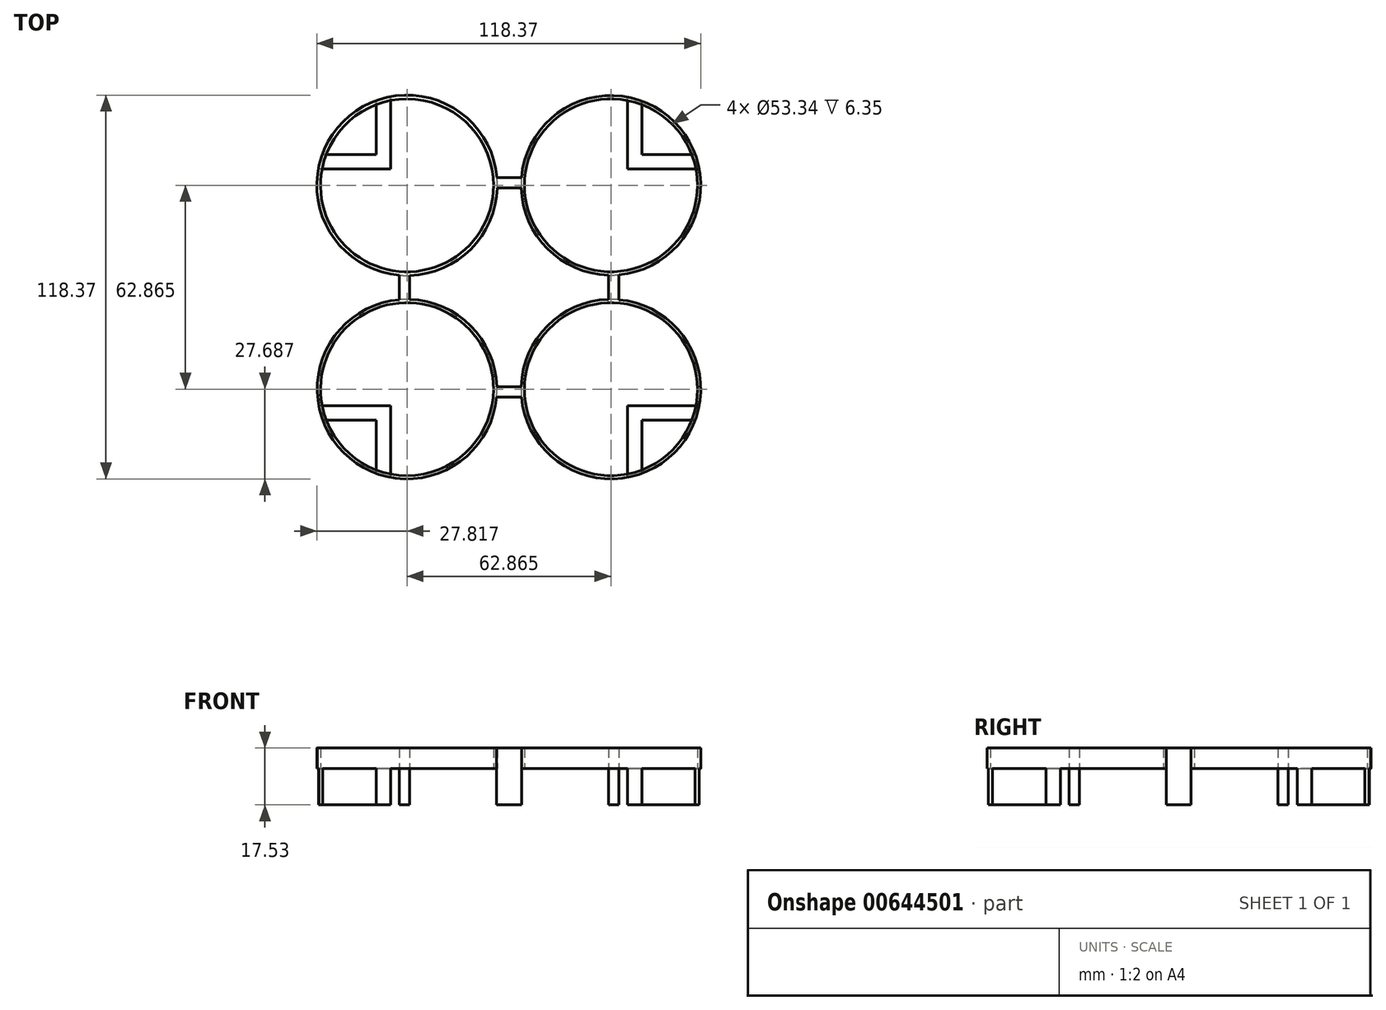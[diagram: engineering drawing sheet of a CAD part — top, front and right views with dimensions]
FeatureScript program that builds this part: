
annotation { "Feature Type Name" : "Feature", "Feature Type Description" : "" }
export const myFeature = defineFeature(function(context is Context, id is Id, definition is map)
    precondition{}
    {
        {
            var Q0;
            Q0=qCreatedBy(makeId("Top.planeOp"),FACE);
            var sketch = newSketch(context, id + "F0", { "sketchPlane" : qUnion([Q0])});
            skCircle(sketch, "E0", {"center": v(-31.43, 31.43) * mm, "radius": 26.67 * mm});
            skCircle(sketch, "E1", {"center": v(31.43, 31.43) * mm, "radius": 26.67 * mm});
            skCircle(sketch, "E2", {"center": v(31.43, -31.43) * mm, "radius": 26.67 * mm});
            skCircle(sketch, "E3", {"center": v(-31.43, -31.43) * mm, "radius": 26.67 * mm});
            skCircle(sketch, "E4", {"center": v(-31.43, 31.43) * mm, "radius": 27.81 * mm});
            skCircle(sketch, "E5", {"center": v(31.43, 31.43) * mm, "radius": 27.69 * mm});
            skCircle(sketch, "E6", {"center": v(31.43, -31.43) * mm, "radius": 27.69 * mm});
            skCircle(sketch, "E7", {"center": v(-31.43, -31.43) * mm, "radius": 27.69 * mm});
            skLineSegment(sketch, "E8.bottom", {"start": v(33.81, 33.81) * mm, "end": v(-33.81, 33.81) * mm});
            skLineSegment(sketch, "E8.top", {"start": v(33.81, -33.81) * mm, "end": v(-33.81, -33.81) * mm});
            skLineSegment(sketch, "E8.left", {"start": v(33.81, 33.81) * mm, "end": v(33.81, -33.81) * mm});
            skLineSegment(sketch, "E8.right", {"start": v(-33.81, 33.81) * mm, "end": v(-33.81, -33.81) * mm});
            skPoint(sketch, "E8.middle", {"position": v(0, 0) * mm});
            skLineSegment(sketch, "E9.bottom", {"start": v(30.64, 30.64) * mm, "end": v(-30.64, 30.64) * mm});
            skLineSegment(sketch, "E9.top", {"start": v(30.64, -30.64) * mm, "end": v(-30.64, -30.64) * mm});
            skLineSegment(sketch, "E9.left", {"start": v(30.64, 30.64) * mm, "end": v(30.64, -30.64) * mm});
            skLineSegment(sketch, "E9.right", {"start": v(-30.64, 30.64) * mm, "end": v(-30.64, -30.64) * mm});
            skSolve(sketch);
        }
        {
            var Q0;
            Q0 = qSketchRegion(id + "F0", true);
            var Q1;
            {var subQ0=sQuery(id+"F0.wireOp",EDGE,"E9.right");var subQ1=sQuery(id+"F0.wireOp",EDGE,"E0");var subQ2=makeQuery(id+"F0.imprint","INTERSECT",VERTEX,{"derivedFrom":[subQ1,subQ0]});Q1=makeQuery(id+"F0.imprint","IMPRINT",FACE,{"disambiguationData":[TD([[makeQuery(id+"F0.imprint","IMPRINT",EDGE,{"disambiguationData":[TD([[subQ2,-1.0]])],"derivedFrom":subQ1}),-1.0]])]});}
            var Q2;
            {var subQ0=sQuery(id+"F0.wireOp",EDGE,"E9.right");var subQ1=sQuery(id+"F0.wireOp",EDGE,"E3");var subQ2=makeQuery(id+"F0.imprint","INTERSECT",VERTEX,{"derivedFrom":[subQ1,subQ0]});Q2=makeQuery(id+"F0.imprint","IMPRINT",FACE,{"disambiguationData":[TD([[makeQuery(id+"F0.imprint","IMPRINT",EDGE,{"disambiguationData":[TD([[subQ2,1.0]])],"derivedFrom":subQ1}),-1.0]])]});}
            var Q3;
            {var subQ0=sQuery(id+"F0.wireOp",EDGE,"E9.left");var subQ1=sQuery(id+"F0.wireOp",EDGE,"E2");var subQ2=makeQuery(id+"F0.imprint","INTERSECT",VERTEX,{"derivedFrom":[subQ1,subQ0]});Q3=makeQuery(id+"F0.imprint","IMPRINT",FACE,{"disambiguationData":[TD([[makeQuery(id+"F0.imprint","IMPRINT",EDGE,{"disambiguationData":[TD([[subQ2,-1.0]])],"derivedFrom":subQ1}),-1.0]])]});}
            var Q4;
            {var subQ0=sQuery(id+"F0.wireOp",EDGE,"E9.bottom");var subQ1=sQuery(id+"F0.wireOp",EDGE,"E1");var subQ2=makeQuery(id+"F0.imprint","INTERSECT",VERTEX,{"derivedFrom":[subQ1,subQ0]});Q4=makeQuery(id+"F0.imprint","IMPRINT",FACE,{"disambiguationData":[TD([[makeQuery(id+"F0.imprint","IMPRINT",EDGE,{"disambiguationData":[TD([[subQ2,-1.0]])],"derivedFrom":subQ1}),-1.0]])]});}
            extrude(context, id + "F1", {"entities" : qUnion([Q0, Q1, Q2, Q3, Q4]), "depth" : 6.35 * mm, "offsetDistance" : 25.4 * mm});
        }
        {
            var Q0;
            {var subQ0=sQuery(id+"F0.wireOp",EDGE,"E8.top");var subQ1=sQuery(id+"F0.wireOp",EDGE,"E6");var subQ2=makeQuery(id+"F0.imprint","INTERSECT",VERTEX,{"derivedFrom":[subQ1,subQ0]});Q0=makeQuery(id+"F0.imprint","IMPRINT",FACE,{"disambiguationData":[TD([[makeQuery(id+"F0.imprint","IMPRINT",EDGE,{"disambiguationData":[TD([[subQ2,1.0]])],"derivedFrom":subQ1}),-1.0]])]});}
            var Q1;
            {var subQ0=sQuery(id+"F0.wireOp",EDGE,"E8.right");var subQ1=sQuery(id+"F0.wireOp",EDGE,"E4");var subQ2=makeQuery(id+"F0.imprint","INTERSECT",VERTEX,{"derivedFrom":[subQ1,subQ0]});Q1=makeQuery(id+"F0.imprint","IMPRINT",FACE,{"disambiguationData":[TD([[makeQuery(id+"F0.imprint","IMPRINT",EDGE,{"disambiguationData":[TD([[subQ2,-1.0]])],"derivedFrom":subQ1}),-1.0]])]});}
            var Q2;
            {var subQ0=sQuery(id+"F0.wireOp",EDGE,"E8.bottom");var subQ1=sQuery(id+"F0.wireOp",EDGE,"E4");var subQ2=makeQuery(id+"F0.imprint","INTERSECT",VERTEX,{"derivedFrom":[subQ1,subQ0]});Q2=makeQuery(id+"F0.imprint","IMPRINT",FACE,{"disambiguationData":[TD([[makeQuery(id+"F0.imprint","IMPRINT",EDGE,{"disambiguationData":[TD([[subQ2,1.0]])],"derivedFrom":subQ1}),-1.0]])]});}
            var Q3;
            {var subQ0=sQuery(id+"F0.wireOp",EDGE,"E8.left");var subQ1=sQuery(id+"F0.wireOp",EDGE,"E5");var subQ2=makeQuery(id+"F0.imprint","INTERSECT",VERTEX,{"derivedFrom":[subQ1,subQ0]});Q3=makeQuery(id+"F0.imprint","IMPRINT",FACE,{"disambiguationData":[TD([[makeQuery(id+"F0.imprint","IMPRINT",EDGE,{"disambiguationData":[TD([[subQ2,1.0]])],"derivedFrom":subQ1}),-1.0]])]});}
            extrude(context, id + "F2", {"entities" : qUnion([Q0, Q1, Q2, Q3]), "operationType" : NewBodyOperationType.ADD, "oppositeDirection" : true, "depth" : 11.18 * mm, "offsetDistance" : 25.4 * mm});
        }
        {
            var Q0;
            Q0=qCreatedBy(makeId("Top.planeOp"),FACE);
            var sketch = newSketch(context, id + "F3", { "sketchPlane" : qUnion([Q0])});
            skLineSegment(sketch, "E10.bottom", {"start": v(-38.75, -38.75) * mm, "end": v(-84.47, -38.75) * mm});
            skLineSegment(sketch, "E10.top", {"start": v(-38.75, -84.47) * mm, "end": v(-84.47, -84.47) * mm});
            skLineSegment(sketch, "E10.left", {"start": v(-38.75, -38.75) * mm, "end": v(-38.75, -84.47) * mm});
            skLineSegment(sketch, "E10.right", {"start": v(-84.47, -38.75) * mm, "end": v(-84.47, -84.47) * mm});
            skPoint(sketch, "E10.middle", {"position": v(-61.6, -61.6) * mm});
            skLineSegment(sketch, "E11.bottom", {"start": v(84.47, -84.47) * mm, "end": v(38.75, -84.47) * mm});
            skLineSegment(sketch, "E11.top", {"start": v(84.47, -38.75) * mm, "end": v(38.75, -38.75) * mm});
            skLineSegment(sketch, "E11.left", {"start": v(84.47, -84.47) * mm, "end": v(84.47, -38.75) * mm});
            skLineSegment(sketch, "E11.right", {"start": v(38.75, -84.47) * mm, "end": v(38.75, -38.75) * mm});
            skPoint(sketch, "E11.middle", {"position": v(61.6, -61.6) * mm});
            skLineSegment(sketch, "E12.bottom", {"start": v(84.47, 38.76) * mm, "end": v(38.75, 38.76) * mm});
            skLineSegment(sketch, "E12.top", {"start": v(84.47, 84.48) * mm, "end": v(38.75, 84.48) * mm});
            skLineSegment(sketch, "E12.left", {"start": v(84.47, 38.76) * mm, "end": v(84.47, 84.48) * mm});
            skLineSegment(sketch, "E12.right", {"start": v(38.75, 38.76) * mm, "end": v(38.75, 84.48) * mm});
            skPoint(sketch, "E12.middle", {"position": v(61.6, 61.62) * mm});
            skLineSegment(sketch, "E13.bottom", {"start": v(-38.75, 38.76) * mm, "end": v(-84.47, 38.76) * mm});
            skLineSegment(sketch, "E13.top", {"start": v(-38.75, 84.48) * mm, "end": v(-84.47, 84.48) * mm});
            skLineSegment(sketch, "E13.left", {"start": v(-38.75, 38.76) * mm, "end": v(-38.75, 84.48) * mm});
            skLineSegment(sketch, "E13.right", {"start": v(-84.47, 38.76) * mm, "end": v(-84.47, 84.48) * mm});
            skPoint(sketch, "E13.middle", {"position": v(-61.6, 61.62) * mm});
            skLineSegment(sketch, "E14.bottom", {"start": v(-36.53, -86.7) * mm, "end": v(-86.7, -86.7) * mm});
            skLineSegment(sketch, "E14.top", {"start": v(-36.53, -36.53) * mm, "end": v(-86.7, -36.53) * mm});
            skLineSegment(sketch, "E14.left", {"start": v(-36.53, -86.7) * mm, "end": v(-36.53, -36.53) * mm});
            skLineSegment(sketch, "E14.right", {"start": v(-86.7, -86.7) * mm, "end": v(-86.7, -36.53) * mm});
            skLineSegment(sketch, "E15.bottom", {"start": v(-40.97, -82.25) * mm, "end": v(-82.25, -82.25) * mm});
            skLineSegment(sketch, "E15.top", {"start": v(-40.97, -40.97) * mm, "end": v(-82.25, -40.97) * mm});
            skLineSegment(sketch, "E15.left", {"start": v(-40.97, -82.25) * mm, "end": v(-40.97, -40.97) * mm});
            skLineSegment(sketch, "E15.right", {"start": v(-82.25, -82.25) * mm, "end": v(-82.25, -40.97) * mm});
            skLineSegment(sketch, "E16.bottom", {"start": v(86.7, -86.7) * mm, "end": v(36.53, -86.7) * mm});
            skLineSegment(sketch, "E16.top", {"start": v(86.7, -36.53) * mm, "end": v(36.53, -36.53) * mm});
            skLineSegment(sketch, "E16.left", {"start": v(86.7, -86.7) * mm, "end": v(86.7, -36.53) * mm});
            skLineSegment(sketch, "E16.right", {"start": v(36.53, -86.7) * mm, "end": v(36.53, -36.53) * mm});
            skLineSegment(sketch, "E17.bottom", {"start": v(82.25, -82.25) * mm, "end": v(40.97, -82.25) * mm});
            skLineSegment(sketch, "E17.top", {"start": v(82.25, -40.97) * mm, "end": v(40.97, -40.97) * mm});
            skLineSegment(sketch, "E17.left", {"start": v(82.25, -82.25) * mm, "end": v(82.25, -40.97) * mm});
            skLineSegment(sketch, "E17.right", {"start": v(40.97, -82.25) * mm, "end": v(40.97, -40.97) * mm});
            skLineSegment(sketch, "E18.bottom", {"start": v(82.25, 40.98) * mm, "end": v(40.97, 40.98) * mm});
            skLineSegment(sketch, "E18.top", {"start": v(82.25, 82.25) * mm, "end": v(40.97, 82.25) * mm});
            skLineSegment(sketch, "E18.left", {"start": v(82.25, 40.98) * mm, "end": v(82.25, 82.25) * mm});
            skLineSegment(sketch, "E18.right", {"start": v(40.97, 40.98) * mm, "end": v(40.97, 82.25) * mm});
            skLineSegment(sketch, "E19.bottom", {"start": v(86.7, 36.53) * mm, "end": v(36.53, 36.53) * mm});
            skLineSegment(sketch, "E19.top", {"start": v(86.7, 86.7) * mm, "end": v(36.53, 86.7) * mm});
            skLineSegment(sketch, "E19.left", {"start": v(86.7, 36.53) * mm, "end": v(86.7, 86.7) * mm});
            skLineSegment(sketch, "E19.right", {"start": v(36.53, 36.53) * mm, "end": v(36.53, 86.7) * mm});
            skLineSegment(sketch, "E20.bottom", {"start": v(-40.97, 40.98) * mm, "end": v(-82.25, 40.98) * mm});
            skLineSegment(sketch, "E20.top", {"start": v(-40.97, 82.25) * mm, "end": v(-82.25, 82.25) * mm});
            skLineSegment(sketch, "E20.left", {"start": v(-40.97, 40.98) * mm, "end": v(-40.97, 82.25) * mm});
            skLineSegment(sketch, "E20.right", {"start": v(-82.25, 40.98) * mm, "end": v(-82.25, 82.25) * mm});
            skLineSegment(sketch, "E21.bottom", {"start": v(-36.53, 36.53) * mm, "end": v(-86.7, 36.53) * mm});
            skLineSegment(sketch, "E21.top", {"start": v(-36.53, 86.7) * mm, "end": v(-86.7, 86.7) * mm});
            skLineSegment(sketch, "E21.left", {"start": v(-36.53, 36.53) * mm, "end": v(-36.53, 86.7) * mm});
            skLineSegment(sketch, "E21.right", {"start": v(-86.7, 36.53) * mm, "end": v(-86.7, 86.7) * mm});
            skCircle(sketch, "E22", {"center": v(-31.43, -31.43) * mm, "radius": 27.69 * mm});
            skCircle(sketch, "E23", {"center": v(31.43, -31.43) * mm, "radius": 27.69 * mm});
            skCircle(sketch, "E24", {"center": v(31.43, 31.43) * mm, "radius": 27.69 * mm});
            skCircle(sketch, "E25", {"center": v(-31.43, 31.43) * mm, "radius": 27.81 * mm});
            skSolve(sketch);
        }
        {
            var Q0;
            {var subQ6=sQuery(id+"F3.wireOp",EDGE,"E13.left");var subQ7=sQuery(id+"F3.wireOp",EDGE,"E13.bottom");var subQ8=makeQuery(id+"F3.imprint","INTERSECT",VERTEX,{"derivedFrom":[subQ7,subQ6]});Q0=makeQuery(id+"F3.imprint","IMPRINT",FACE,{"disambiguationData":[TD([[makeQuery(id+"F3.imprint","IMPRINT",EDGE,{"disambiguationData":[TD([[subQ8,-1.0]])],"derivedFrom":subQ7}),1.0]])]});}
            var Q1;
            {var subQ5=sQuery(id+"F3.wireOp",EDGE,"E13.bottom");var subQ7=sQuery(id+"F3.wireOp",EDGE,"E13.left");var subQ8=makeQuery(id+"F3.imprint","INTERSECT",VERTEX,{"derivedFrom":[subQ5,subQ7]});Q1=makeQuery(id+"F3.imprint","IMPRINT",FACE,{"disambiguationData":[TD([[makeQuery(id+"F3.imprint","IMPRINT",EDGE,{"disambiguationData":[TD([[subQ8,-1.0]])],"derivedFrom":subQ5}),-1.0]])]});}
            var Q2;
            {var subQ6=sQuery(id+"F3.wireOp",EDGE,"E12.right");var subQ8=sQuery(id+"F3.wireOp",EDGE,"E12.bottom");var subQ9=makeQuery(id+"F3.imprint","INTERSECT",VERTEX,{"derivedFrom":[subQ8,subQ6]});Q2=makeQuery(id+"F3.imprint","IMPRINT",FACE,{"disambiguationData":[TD([[makeQuery(id+"F3.imprint","IMPRINT",EDGE,{"disambiguationData":[TD([[subQ9,1.0]])],"derivedFrom":subQ8}),1.0]])]});}
            var Q3;
            {var subQ5=sQuery(id+"F3.wireOp",EDGE,"E12.bottom");var subQ8=sQuery(id+"F3.wireOp",EDGE,"E12.right");var subQ9=makeQuery(id+"F3.imprint","INTERSECT",VERTEX,{"derivedFrom":[subQ5,subQ8]});Q3=makeQuery(id+"F3.imprint","IMPRINT",FACE,{"disambiguationData":[TD([[makeQuery(id+"F3.imprint","IMPRINT",EDGE,{"disambiguationData":[TD([[subQ9,1.0]])],"derivedFrom":subQ5}),-1.0]])]});}
            var Q4;
            {var subQ6=sQuery(id+"F3.wireOp",EDGE,"E10.bottom");var subQ8=sQuery(id+"F3.wireOp",EDGE,"E10.left");var subQ9=makeQuery(id+"F3.imprint","INTERSECT",VERTEX,{"derivedFrom":[subQ6,subQ8]});Q4=makeQuery(id+"F3.imprint","IMPRINT",FACE,{"disambiguationData":[TD([[makeQuery(id+"F3.imprint","IMPRINT",EDGE,{"disambiguationData":[TD([[subQ9,-1.0]])],"derivedFrom":subQ6}),-1.0]])]});}
            var Q5;
            {var subQ6=sQuery(id+"F3.wireOp",EDGE,"E10.left");var subQ8=sQuery(id+"F3.wireOp",EDGE,"E10.bottom");var subQ9=makeQuery(id+"F3.imprint","INTERSECT",VERTEX,{"derivedFrom":[subQ8,subQ6]});Q5=makeQuery(id+"F3.imprint","IMPRINT",FACE,{"disambiguationData":[TD([[makeQuery(id+"F3.imprint","IMPRINT",EDGE,{"disambiguationData":[TD([[subQ9,-1.0]])],"derivedFrom":subQ8}),1.0]])]});}
            var Q6;
            {var subQ5=sQuery(id+"F3.wireOp",EDGE,"E11.right");var subQ6=sQuery(id+"F3.wireOp",EDGE,"E11.top");var subQ7=makeQuery(id+"F3.imprint","INTERSECT",VERTEX,{"derivedFrom":[subQ6,subQ5]});Q6=makeQuery(id+"F3.imprint","IMPRINT",FACE,{"disambiguationData":[TD([[makeQuery(id+"F3.imprint","IMPRINT",EDGE,{"disambiguationData":[TD([[subQ7,1.0]])],"derivedFrom":subQ6}),-1.0]])]});}
            var Q7;
            {var subQ6=sQuery(id+"F3.wireOp",EDGE,"E11.right");var subQ7=sQuery(id+"F3.wireOp",EDGE,"E11.top");var subQ8=makeQuery(id+"F3.imprint","INTERSECT",VERTEX,{"derivedFrom":[subQ7,subQ6]});Q7=makeQuery(id+"F3.imprint","IMPRINT",FACE,{"disambiguationData":[TD([[makeQuery(id+"F3.imprint","IMPRINT",EDGE,{"disambiguationData":[TD([[subQ8,1.0]])],"derivedFrom":subQ7}),1.0]])]});}
            extrude(context, id + "F4", {"entities" : qUnion([Q0, Q1, Q2, Q3, Q4, Q5, Q6, Q7]), "operationType" : NewBodyOperationType.ADD, "oppositeDirection" : true, "depth" : 11.18 * mm, "offsetDistance" : 25.4 * mm});
        }
    });
